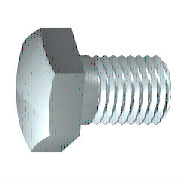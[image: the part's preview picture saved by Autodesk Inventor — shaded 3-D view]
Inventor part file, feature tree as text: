
AUTODESK INVENTOR PART (.ipt)
format: ipt  version: 2025.1 (Build 291241020, 241B)  size: 197,120 bytes
history: native  units: mm (DEFAULTED — no unit token found)
features: extrude x1, chamfer x1, plane x1
ambient origin geometry x7: Origin, YZ Plane, XZ Plane, X Axis, Y Axis, Z Axis, Center Point
bodies: Solid1 (feature_tree), Body (feature_tree)
feature tree (3):
  extrude  "Head"  Depth=40.0mm
  chamfer  "Chamfer1"  Distance=35.5mm
  plane  "Work Plane1"
